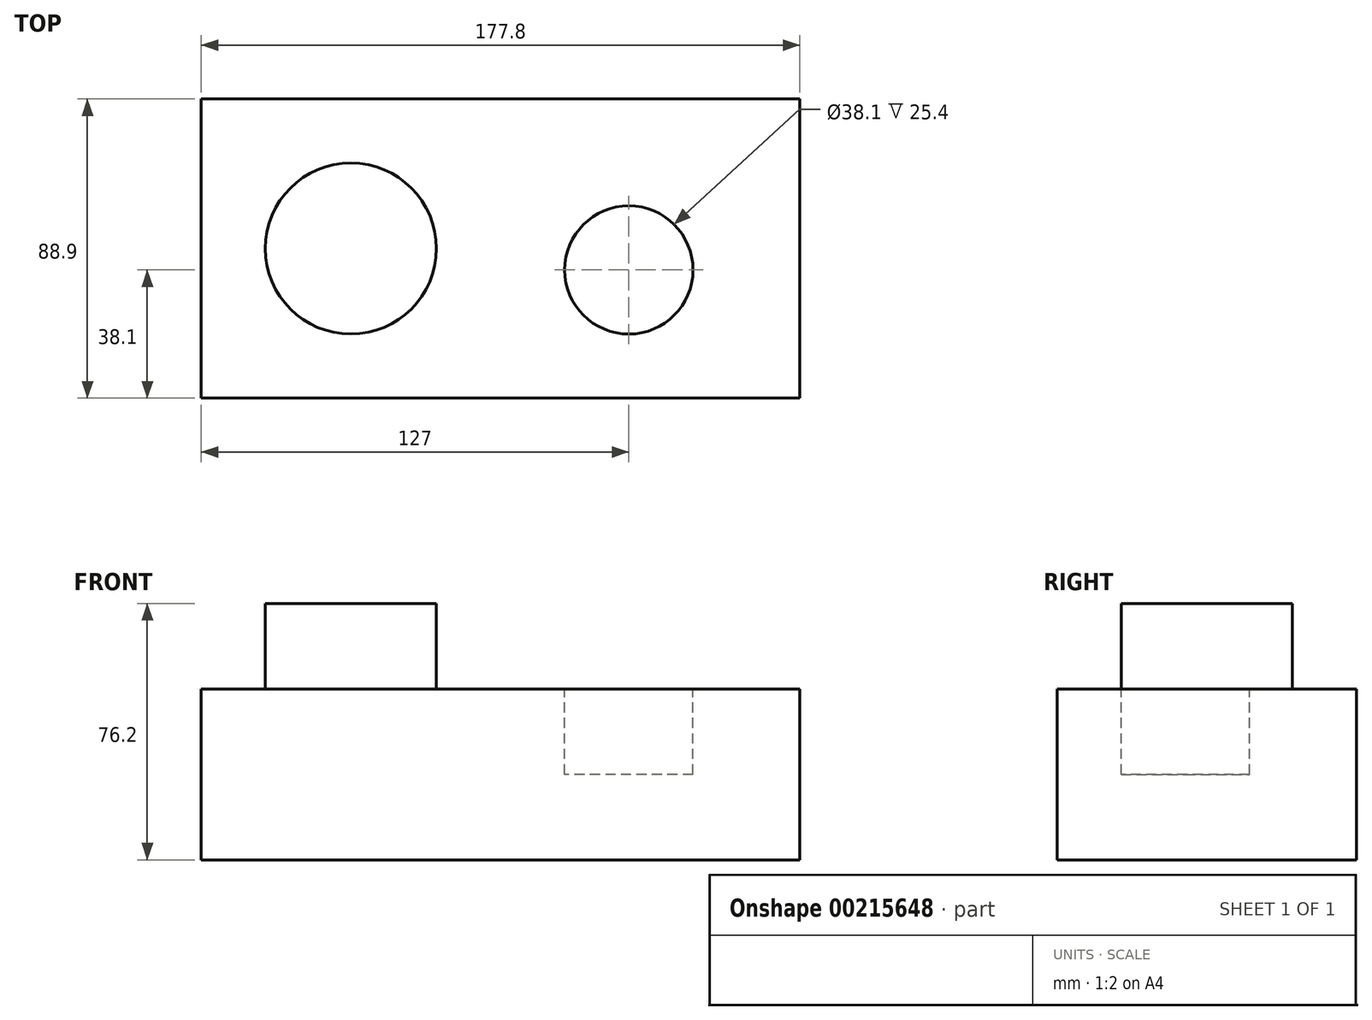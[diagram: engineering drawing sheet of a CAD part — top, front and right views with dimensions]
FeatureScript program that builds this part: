
annotation { "Feature Type Name" : "Feature", "Feature Type Description" : "" }
export const myFeature = defineFeature(function(context is Context, id is Id, definition is map)
    precondition{}
    {
        {
            var Q0;
            Q0=qCreatedBy(makeId("Top.planeOp"),FACE);
            var sketch = newSketch(context, id + "F0", { "sketchPlane" : qUnion([Q0])});
            skLineSegment(sketch, "E0.bottom", {"start": v(0, 0) * mm, "end": v(177.8, 0) * mm});
            skLineSegment(sketch, "E0.top", {"start": v(0, 88.9) * mm, "end": v(177.8, 88.9) * mm});
            skLineSegment(sketch, "E0.left", {"start": v(0, 0) * mm, "end": v(0, 88.9) * mm});
            skLineSegment(sketch, "E0.right", {"start": v(177.8, 0) * mm, "end": v(177.8, 88.9) * mm});
            skSolve(sketch);
        }
        {
            var Q0;
            Q0 = qSketchRegion(id + "F0", true);
            extrude(context, id + "F1", {"entities" : qUnion([Q0]), "depth" : 50.8 * mm});
        }
        {
            var Q0;
            Q0=makeQuery(id+"F1.opExtrude","CAP_FACE",FACE,{"disambiguationData":[OSD([sQuery(id+"F0.wireOp",EDGE,"E0.bottom"),sQuery(id+"F0.wireOp",EDGE,"E0.top"),sQuery(id+"F0.wireOp",EDGE,"E0.left"),sQuery(id+"F0.wireOp",EDGE,"E0.right")])],"isStart":false});
            var sketch = newSketch(context, id + "F2", { "sketchPlane" : qUnion([Q0])});
            skCircle(sketch, "E1", {"center": v(44.45, 44.45) * mm, "radius": 25.4 * mm});
            skSolve(sketch);
        }
        {
            var Q0;
            Q0 = qSketchRegion(id + "F2", true);
            extrude(context, id + "F3", {"entities" : qUnion([Q0]), "operationType" : NewBodyOperationType.ADD, "depth" : 25.4 * mm});
        }
        {
            var Q0;
            Q0=makeQuery(id+"F1.opExtrude","CAP_FACE",FACE,{"disambiguationData":[OSD([sQuery(id+"F0.wireOp",EDGE,"E0.bottom"),sQuery(id+"F0.wireOp",EDGE,"E0.top"),sQuery(id+"F0.wireOp",EDGE,"E0.left"),sQuery(id+"F0.wireOp",EDGE,"E0.right")])],"isStart":false});
            var sketch = newSketch(context, id + "F4", { "sketchPlane" : qUnion([Q0])});
            skCircle(sketch, "E2", {"center": v(127, 38.1) * mm, "radius": 19.05 * mm});
            skSolve(sketch);
        }
        {
            var Q0;
            Q0 = qSketchRegion(id + "F4", true);
            extrude(context, id + "F5", {"entities" : qUnion([Q0]), "operationType" : NewBodyOperationType.REMOVE, "oppositeDirection" : true, "depth" : 25.4 * mm});
        }
    });
